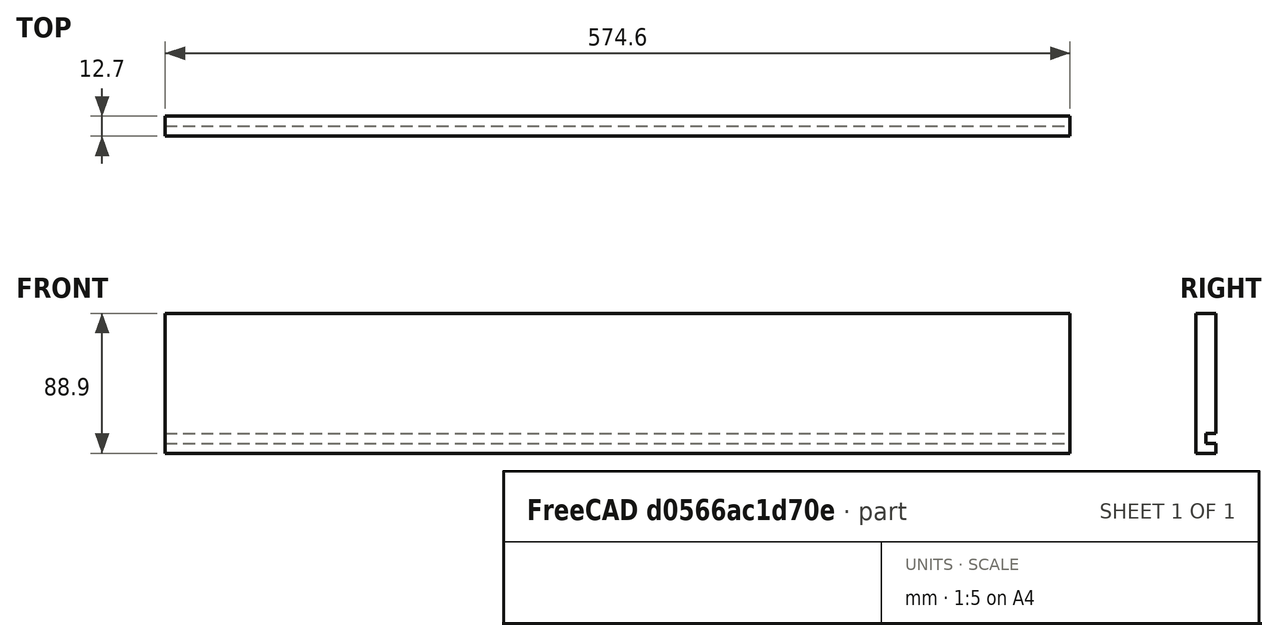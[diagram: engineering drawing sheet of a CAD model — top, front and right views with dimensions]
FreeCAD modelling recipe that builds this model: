
FCSTD DOCUMENT  (FreeCAD 0.19R24291 (Git))
Label: side2
License: All rights reserved
LicenseURL: http://en.wikipedia.org/wiki/All_rights_reserved
objects: Sketcher::SketchObject×1, PartDesign::Pad×1, PartDesign::Body×1
note: 4 computed .brp shape members not serialized (recipe doc carries the construction recipe); baked Part::Feature solids carry a one-line shape summary decoded from their .brp

FEATURE [Sketcher::SketchObject] Sketch
  FullyConstrained = true
  MapMode = 5
  Placement = pos=(0,0,0) rot=(0.57735,0.57735,0.57735;2.0944rad)
  Support = -> [YZ_Plane]
  expr: Constraints[20] = 1 / 4 * 25.4
  expr: Constraints[7] = 0.5 * 25.4
  expr: Constraints[5] = 3.5 * 25.4
  sketch-geometry (8):
    g0: LineSegment StartX=0 StartY=0 StartZ=0 EndX=12.7 EndY=0 EndZ=0
    g1: LineSegment StartX=12.7 StartY=88.9 StartZ=0 EndX=0 EndY=88.9 EndZ=0
    g2: LineSegment StartX=0 StartY=88.9 StartZ=0 EndX=0 EndY=0 EndZ=0
    g3: LineSegment StartX=12.7 StartY=0 StartZ=0 EndX=12.7 EndY=6.35 EndZ=0
    g4: LineSegment StartX=12.7 StartY=6.35 StartZ=0 EndX=6.35 EndY=6.35 EndZ=0
    g5: LineSegment StartX=6.35 StartY=6.35 StartZ=0 EndX=6.35 EndY=12.7 EndZ=0
    g6: LineSegment StartX=6.35 StartY=12.7 StartZ=0 EndX=12.7 EndY=12.7 EndZ=0
    g7: LineSegment StartX=12.7 StartY=12.7 StartZ=0 EndX=12.7 EndY=88.9 EndZ=0
  constraints (23):
    c: Coincident(g1,g2)
    c: Coincident(g2,g0)
    c: Horizontal(g0)
    c: Horizontal(g1)
    c: Vertical(g2)
    c: DistanceY(g2,g2) = 88.9
    c: Coincident(g0,g-1)
    c: DistanceX(g0,g0) = 12.7
    c: Coincident(g0,g3)
    c: Vertical(g3)
    c: Coincident(g3,g4)
    c: Coincident(g4,g5)
    c: Coincident(g5,g6)
    c: Horizontal(g6)
    c: Coincident(g6,g7)
    c: Coincident(g7,g1)
    c: Vertical(g7)
    c: Equal(g1,g0)
    c: Parallel(g4,g0)
    c: Parallel(g5,g2)
    c: DistanceY(g3,g3) = 6.35
    c: Equal(g3,g5)
    c: Equal(g3,g4)
FEATURE [PartDesign::Pad] Pad
  Direction = (1,1,1)
  Length = 574.6
  Length2 = 100
  Placement = pos=(0,0,0) rot=(0.57735,0.57735,0.57735;2.0944rad)
  Profile = -> Sketch
  Type = 0
  expr: Length = 600 - (1 / 2 + 1 / 2) * 25.4
FEATURE [PartDesign::Body] Body
  Group = -> [Sketch,Pad]
  Origin = -> Origin
  Tip = -> Pad
